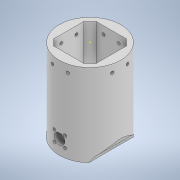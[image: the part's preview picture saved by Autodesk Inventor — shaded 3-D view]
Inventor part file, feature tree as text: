
AUTODESK INVENTOR PART (.ipt)
format: ipt  version: 2021 (Build 250183000, 183)  size: 339,968 bytes
history: native  units: mm
features: sketch x14, extrude x12, chamfer x2
ambient origin geometry x8: Origin, YZ Plane, XZ Plane, XY Plane, X Axis, Y Axis, Z Axis, Center Point
bodies: Body1 (feature_tree)
feature tree (28):
  extrude  "Extrusión2"  Depth=100.0mm TaperAngle=0.0deg
  sketch  "Boceto5"  dims[d45=100.0mm d46=0.0mm d53=10.0mm]
  sketch  "Boceto7"  dims[d54=10.0mm d55=25.0mm]
  extrude  "Extrusión4"  Depth=10.0mm
  extrude  "Extrusión8"  Depth=10.0mm
  extrude  "Extrusión12"  Depth=20.0mm
  extrude  "Extrusión13"  Depth=30.0mm
  sketch  "Boceto14"  dims[d62=200.0mm d63=0.0mm d95=8.0mm]
  extrude  "Extrusión16"  Depth=8.0mm
  extrude  "Extrusión17"  Depth=3.0mm
  extrude  "Extrusión18"  Depth=8.0mm
  extrude  "Extrusión19"  Depth=200.0mm TaperAngle=0.0deg
  extrude  "Extrusión20"  Depth=1000.0mm TaperAngle=0.0deg
  extrude  "Extrusión21"  Depth=1000.0mm TaperAngle=0.0deg
  sketch  "Boceto22"  dims[d151=20.0mm]
  extrude  "Extrusión22"  Depth=1000.0mm TaperAngle=0.0deg
  chamfer  "Chaflán1"  Distance=1000.0mm
  chamfer  "Chaflán2"  Distance=8.0mm
  sketch  "Boceto4"  dims[d20=40.0mm d22=360.0deg d28=100.0mm d29=0.0mm]
  sketch  "Boceto10"  dims[d58=20.0mm d59=20.0mm]
  sketch  "Boceto11"  dims[d60=30.0mm d61=30.0mm]
  sketch  "Boceto15"  dims[d96=8.0mm d97=3.0mm]
  sketch  "Boceto16"  dims[d98=8.0mm d99=8.0mm]
  sketch  "Boceto17"  dims[d100=3.0mm d101=200.0mm d102=0.0mm]
  sketch  "Boceto18"  dims[d111=200.0mm d112=0.0mm d126=1000.0mm d127=0.0mm]
  sketch  "Boceto19"  dims[d128=1000.0mm d129=0.0mm d130=1000.0mm d131=0.0mm]
  sketch  "Boceto21"  dims[d132=1000.0mm d133=0.0mm d134=1000.0mm d135=0.0mm]
  sketch  "Boceto23"  dims[d152=5.0mm d153=1000.0mm d154=0.0mm d155=8.0mm d156=20.0mm d157=0.0mm d158=1.0mm d159=2.0mm d160=45.0deg d161=1.0mm d162=2.0mm d163=45.0deg d11=0.5mm d12=0.872665mm d13=0.5mm d14=0.872665mm d30=0.5mm d31=0.872665mm d36=0.5mm d37=0.872665mm d38=0.5mm d39=0.872665mm d47=0.5mm d48=0.872665mm d49=0.5mm d50=0.872665mm d68=0.5mm d69=0.872665mm d70=0.5mm d71=0.872665mm]
